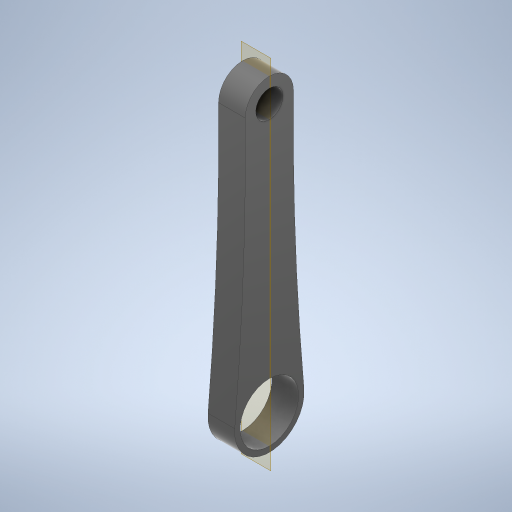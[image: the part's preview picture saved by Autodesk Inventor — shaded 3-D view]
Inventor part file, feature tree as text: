
AUTODESK INVENTOR PART (.ipt)
format: ipt  version: 2023 (Build 270158000, 158)  size: 265,728 bytes
history: native  units: mm
features: extrude x1, plane x1, sketch x1
ambient origin geometry x8: Origin, YZ Plane, XZ Plane, XY Plane, X Axis, Y Axis, Z Axis, Center Point
bodies: Volumenkörper1 (feature_tree)
feature tree (3):
  extrude  "Extrusion1"  Depth=99.913mm
  plane  "Arbeitsebene1"
  sketch  "Skizze1"  dims[d0=26.0mm d1=99.913mm d2=21.9mm d3=18.0mm d6=0.0mm d7=0.0mm d8=0.0mm d9=10.0mm d10=10.0mm d11=10.2mm d12=10.0mm d13=0.0mm d14=0.0mm]
